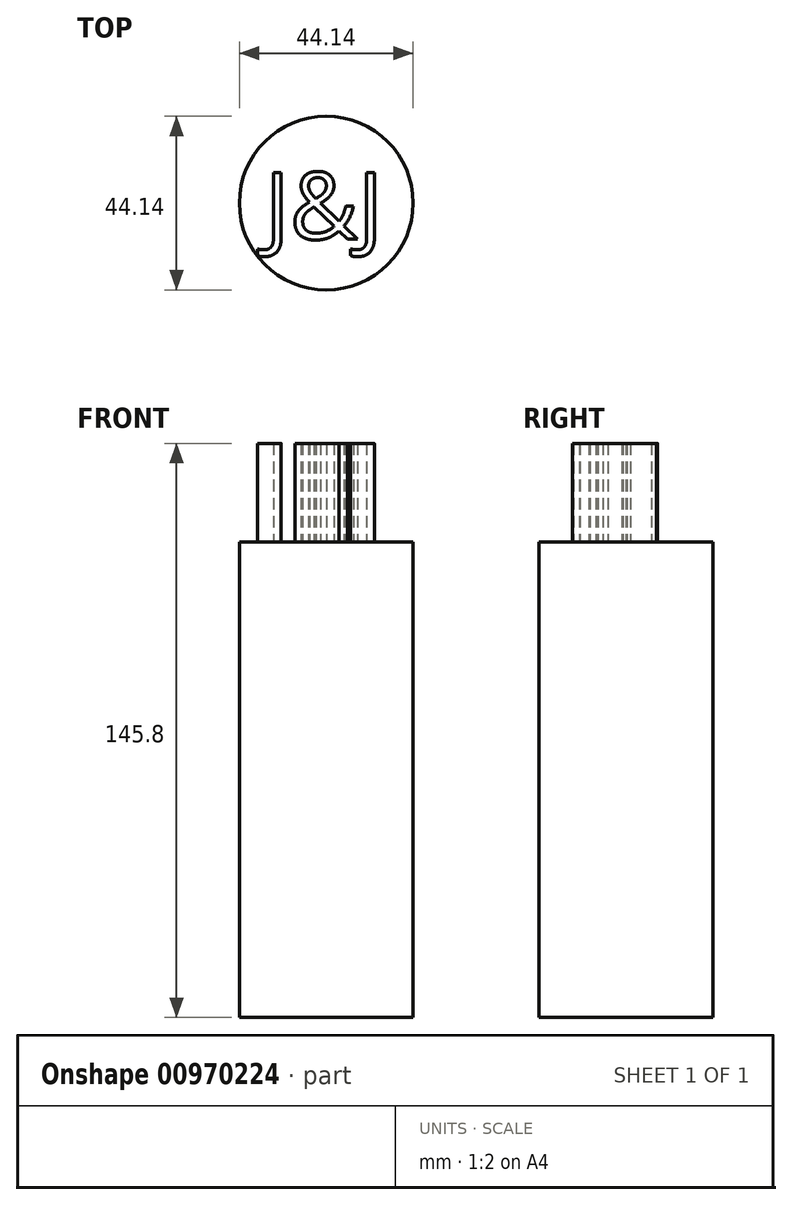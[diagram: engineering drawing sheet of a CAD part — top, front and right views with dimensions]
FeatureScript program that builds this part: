
annotation { "Feature Type Name" : "Feature", "Feature Type Description" : "" }
export const myFeature = defineFeature(function(context is Context, id is Id, definition is map)
    precondition{}
    {
        {
            var Q0;
            Q0=qCreatedBy(makeId("Top.planeOp"),FACE);
            var sketch = newSketch(context, id + "F0", { "sketchPlane" : qUnion([Q0])});
            skCircle(sketch, "E0", {"center": v(0, 0) * mm, "radius": 18.9 * mm});
            skSolve(sketch);
        }
        {
            var Q0;
            Q0=qCreatedBy(makeId("Top.planeOp"),FACE);
            var sketch = newSketch(context, id + "F1", { "sketchPlane" : qUnion([Q0])});
            skCircle(sketch, "E1", {"center": v(0, 0) * mm, "radius": 22.07 * mm});
            skSolve(sketch);
        }
        {
            var Q0;
            Q0=makeQuery(id+"F1.imprint","IMPRINT",FACE,{"disambiguationData":[TD([[makeQuery(id+"F1.imprint","IMPRINT",EDGE,{"derivedFrom":sQuery(id+"F1.wireOp",EDGE,"E1")}),1.0]])]});
            extrude(context, id + "F2", {"entities" : qUnion([Q0]), "depth" : 120.8 * mm, "offsetDistance" : 25 * mm});
        }
        {
            var Q0;
            Q0 = qSketchRegion(id + "F0", true);
            extrude(context, id + "F3", {"entities" : qUnion([Q0]), "operationType" : NewBodyOperationType.ADD, "depth" : 25 * mm, "offsetDistance" : 25 * mm});
        }
        {
            var Q0;
            Q0=makeQuery(id+"F2.opExtrude","CAP_FACE",FACE,{"disambiguationData":[OSD([sQuery(id+"F1.wireOp",EDGE,"E1")])],"isStart":false});
            var sketch = newSketch(context, id + "F4", { "sketchPlane" : qUnion([Q0])});
            skText(sketch, "E2", { "text": "J&J", "fontName": "OpenSans-Regular.ttf"});
            const initialGuessF4  = {"E2": [-0.01563, -0.00917, 1, 0, 0.0171]};
            skSetInitialGuess(sketch, initialGuessF4);
            skSolve(sketch);
        }
        {
            var Q0;
            Q0 = qSketchRegion(id + "F4", true);
            extrude(context, id + "F5", {"entities" : qUnion([Q0]), "operationType" : NewBodyOperationType.ADD, "depth" : 25 * mm, "offsetDistance" : 25 * mm});
        }
    });
